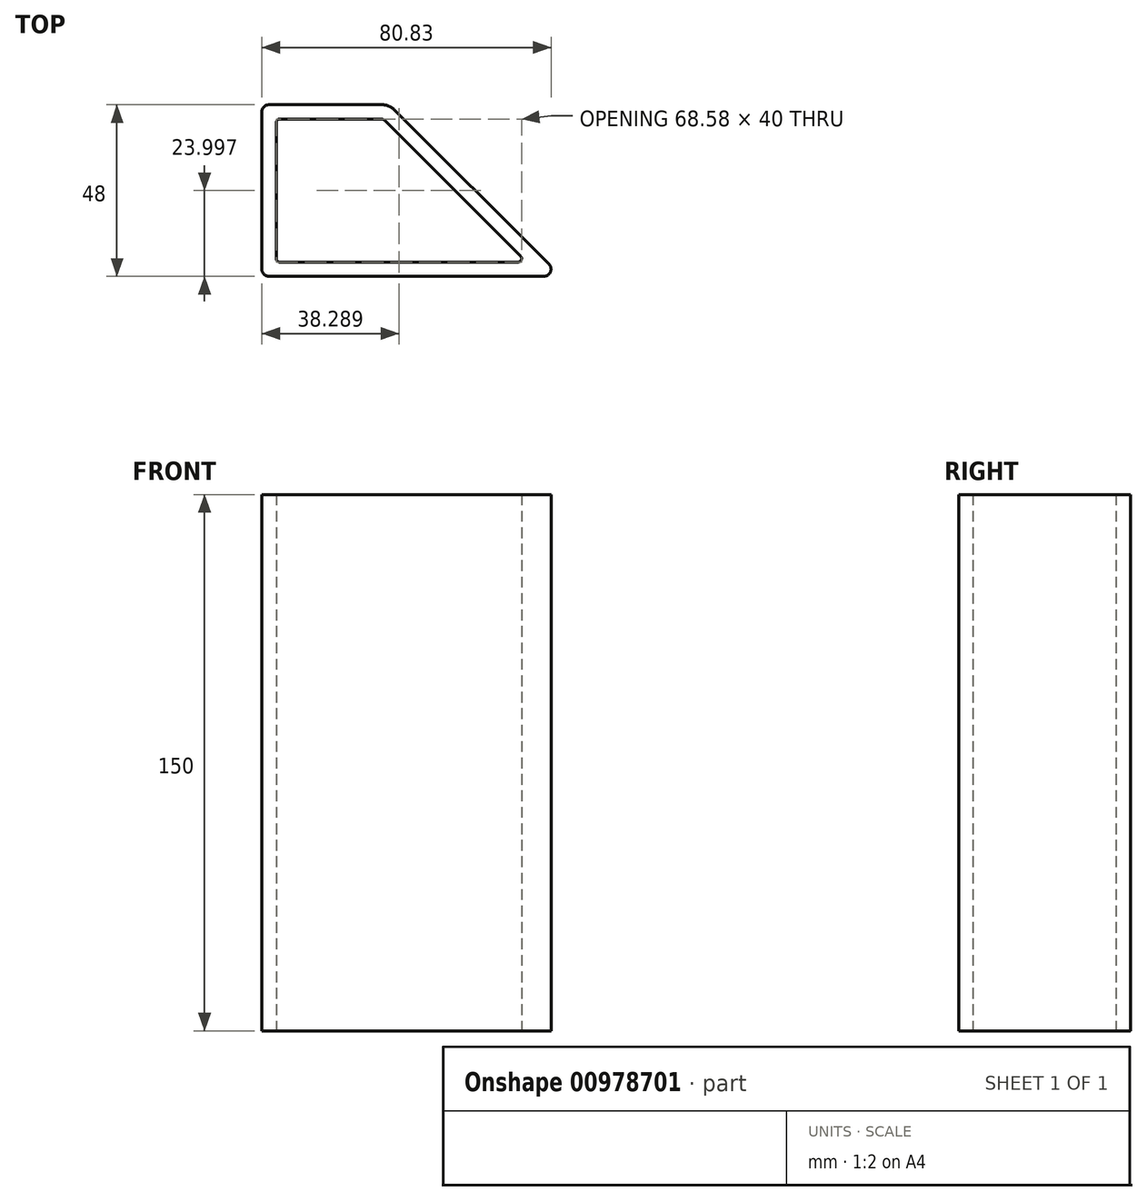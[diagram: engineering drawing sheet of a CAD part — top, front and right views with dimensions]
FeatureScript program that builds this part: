
annotation { "Feature Type Name" : "Feature", "Feature Type Description" : "" }
export const myFeature = defineFeature(function(context is Context, id is Id, definition is map)
    precondition{}
    {
        {
            var Q0;
            Q0=qCreatedBy(makeId("Top.planeOp"),FACE);
            var sketch = newSketch(context, id + "F0", { "sketchPlane" : qUnion([Q0])});
            skLineSegment(sketch, "E0", {"start": v(-67.3, 49.35) * mm, "end": v(-35.7, 49.35) * mm});
            skLineSegment(sketch, "E1", {"start": v(-32.17, 47.88) * mm, "end": v(10.95, 4.76) * mm});
            skLineSegment(sketch, "E2", {"start": v(9.54, 1.35) * mm, "end": v(-67.3, 1.35) * mm});
            skLineSegment(sketch, "E3", {"start": v(-69.3, 3.35) * mm, "end": v(-69.3, 47.35) * mm});
            skLineSegment(sketch, "E4.0", {"start": v(-64.3, 45.35) * mm, "end": v(-36.12, 45.35) * mm});
            skLineSegment(sketch, "E4.1", {"start": v(-65.3, 6.35) * mm, "end": v(-65.3, 44.35) * mm});
            skLineSegment(sketch, "E4.2", {"start": v(2.3, 5.35) * mm, "end": v(-64.3, 5.35) * mm});
            skLineSegment(sketch, "E4.3", {"start": v(-34.7, 44.76) * mm, "end": v(3, 7.05) * mm});
            skPoint(sketch, "E5.visualSharp", {"position": v(-33.63, 49.35) * mm});
            skArc(sketch, "E5.filletArc", {"start": v(-32.17, 47.88) * mm, "mid": v(-33.8, 48.97) * mm, "end": v(-35.7, 49.35) * mm});
            skPoint(sketch, "E6.visualSharp", {"position": v(-69.3, 49.35) * mm});
            skArc(sketch, "E6.filletArc", {"start": v(-67.3, 49.35) * mm, "mid": v(-68.7, 48.76) * mm, "end": v(-69.3, 47.35) * mm});
            skPoint(sketch, "E7.visualSharp", {"position": v(-65.3, 45.35) * mm});
            skArc(sketch, "E7.filletArc", {"start": v(-64.3, 45.35) * mm, "mid": v(-65, 45.05) * mm, "end": v(-65.3, 44.35) * mm});
            skPoint(sketch, "E8.visualSharp", {"position": v(-35.3, 45.35) * mm});
            skArc(sketch, "E8.filletArc", {"start": v(-34.7, 44.76) * mm, "mid": v(-35.35, 45.2) * mm, "end": v(-36.12, 45.35) * mm});
            skPoint(sketch, "E9.visualSharp", {"position": v(-69.3, 1.35) * mm});
            skArc(sketch, "E9.filletArc", {"start": v(-69.3, 3.35) * mm, "mid": v(-68.7, 1.93) * mm, "end": v(-67.3, 1.35) * mm});
            skPoint(sketch, "E10.visualSharp", {"position": v(14.37, 1.35) * mm});
            skArc(sketch, "E10.filletArc", {"start": v(9.54, 1.35) * mm, "mid": v(11.38, 2.58) * mm, "end": v(10.95, 4.76) * mm});
            skPoint(sketch, "E11.visualSharp", {"position": v(-65.3, 5.35) * mm});
            skArc(sketch, "E11.filletArc", {"start": v(-65.3, 6.35) * mm, "mid": v(-65, 5.64) * mm, "end": v(-64.3, 5.35) * mm});
            skPoint(sketch, "E12.visualSharp", {"position": v(4.7, 5.35) * mm});
            skArc(sketch, "E12.filletArc", {"start": v(2.3, 5.35) * mm, "mid": v(3.22, 5.96) * mm, "end": v(3, 7.05) * mm});
            skSolve(sketch);
        }
        {
            var Q0;
            Q0=makeQuery(id+"F0.imprint","IMPRINT",FACE,{"disambiguationData":[TD([[makeQuery(id+"F0.imprint","IMPRINT",EDGE,{"derivedFrom":sQuery(id+"F0.wireOp",EDGE,"E0")}),-1.0]])]});
            extrude(context, id + "F1", {"entities" : qUnion([Q0]), "depth" : 150 * mm, "offsetDistance" : 25 * mm});
        }
    });
